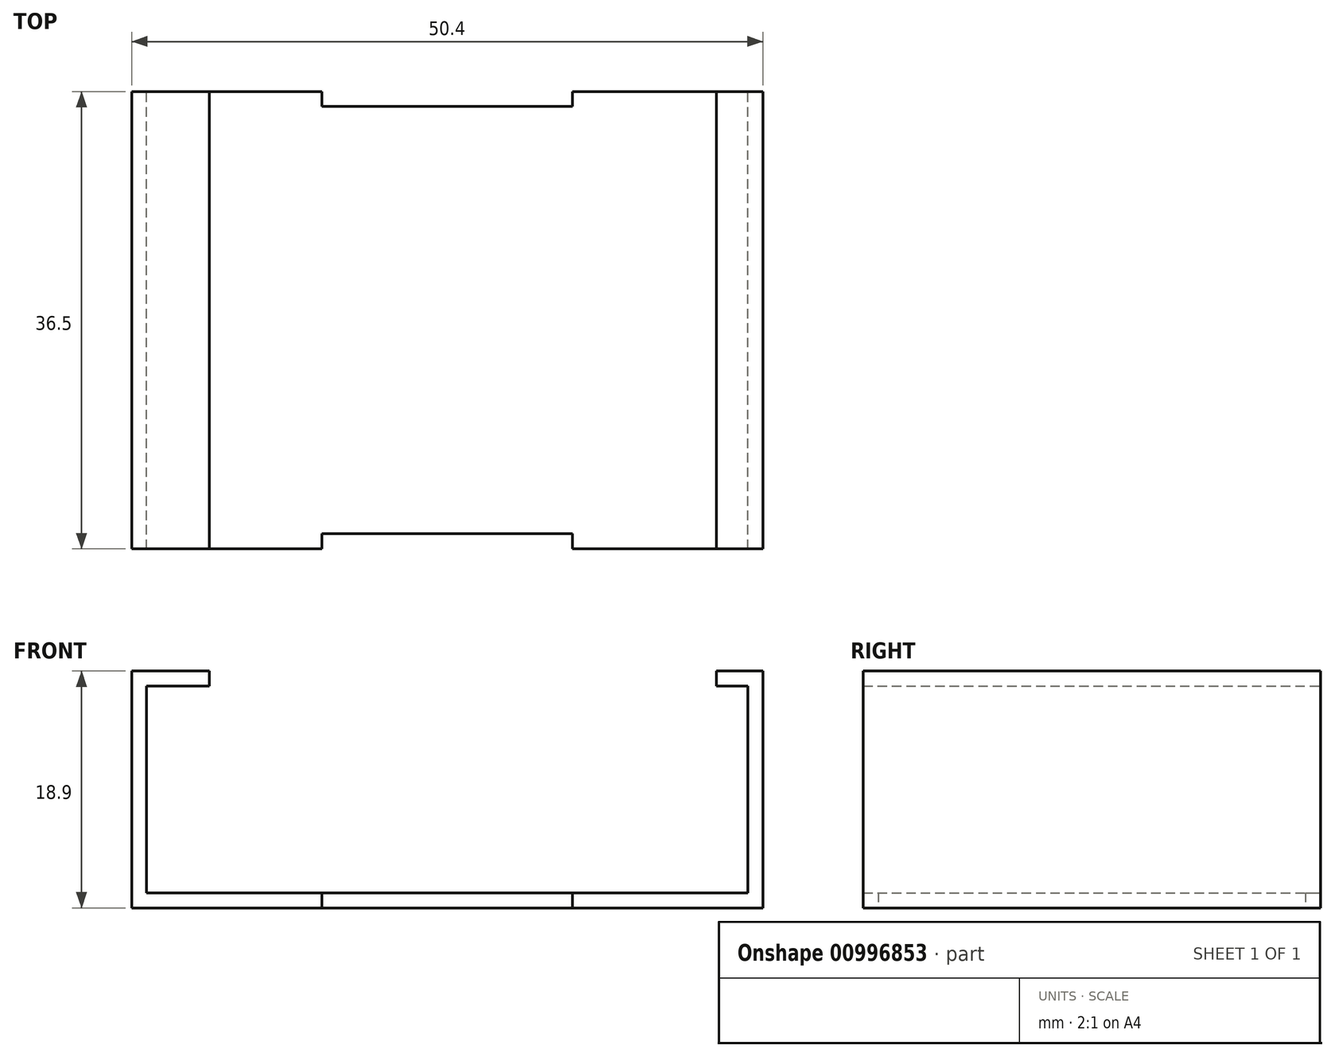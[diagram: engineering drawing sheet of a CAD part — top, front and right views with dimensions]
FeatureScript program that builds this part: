
annotation { "Feature Type Name" : "Feature", "Feature Type Description" : "" }
export const myFeature = defineFeature(function(context is Context, id is Id, definition is map)
    precondition{}
    {
        {
            var Q0;
            Q0=qCreatedBy(makeId("Top.planeOp"),FACE);
            var sketch = newSketch(context, id + "F0", { "sketchPlane" : qUnion([Q0])});
            skLineSegment(sketch, "E0.bottom", {"start": v(24, -18.25) * mm, "end": v(10, -18.25) * mm});
            skLineSegment(sketch, "E0.top", {"start": v(24, 18.25) * mm, "end": v(10, 18.25) * mm});
            skLineSegment(sketch, "E0.left", {"start": v(24, -18.25) * mm, "end": v(24, 18.25) * mm});
            skLineSegment(sketch, "E0.right", {"start": v(-24, -18.25) * mm, "end": v(-24, 18.25) * mm});
            skPoint(sketch, "E0.middle", {"position": v(0, 0) * mm});
            skLineSegment(sketch, "E1.bottom", {"start": v(10, 17.05) * mm, "end": v(-10, 17.05) * mm});
            skLineSegment(sketch, "E1.left", {"start": v(10, 17.05) * mm, "end": v(10, 18.25) * mm});
            skLineSegment(sketch, "E1.right", {"start": v(-10, 17.05) * mm, "end": v(-10, 18.25) * mm});
            skPoint(sketch, "E1.middle", {"position": v(0, 18.25) * mm});
            skLineSegment(sketch, "E2.top", {"start": v(10, -17.05) * mm, "end": v(-10, -17.05) * mm});
            skLineSegment(sketch, "E2.left", {"start": v(10, -18.25) * mm, "end": v(10, -17.05) * mm});
            skLineSegment(sketch, "E2.right", {"start": v(-10, -18.25) * mm, "end": v(-10, -17.05) * mm});
            skPoint(sketch, "E2.middle", {"position": v(0, -18.25) * mm});
            skLineSegment(sketch, "E3.trimOffspring", {"start": v(-10, 18.25) * mm, "end": v(-24, 18.25) * mm});
            skPoint(sketch, "E1.top.end.orphan", {"position": v(-10, 19.45) * mm});
            skPoint(sketch, "E4.orphan", {"position": v(10, 19.45) * mm});
            skPoint(sketch, "E2.bottom.end.orphan", {"position": v(-10, -19.45) * mm});
            skPoint(sketch, "E5.orphan", {"position": v(10, -19.45) * mm});
            skLineSegment(sketch, "E6.trimOffspring", {"start": v(-10, -18.25) * mm, "end": v(-24, -18.25) * mm});
            skLineSegment(sketch, "E7.bottom", {"start": v(24, 18.25) * mm, "end": v(25.2, 18.25) * mm});
            skLineSegment(sketch, "E7.top", {"start": v(24, -18.25) * mm, "end": v(25.2, -18.25) * mm});
            skLineSegment(sketch, "E7.left", {"start": v(24, 18.25) * mm, "end": v(24, -18.25) * mm});
            skLineSegment(sketch, "E7.right", {"start": v(25.2, 18.25) * mm, "end": v(25.2, -18.25) * mm});
            skLineSegment(sketch, "E8.bottom", {"start": v(-24, -18.25) * mm, "end": v(-25.2, -18.25) * mm});
            skLineSegment(sketch, "E8.top", {"start": v(-24, 18.25) * mm, "end": v(-25.2, 18.25) * mm});
            skLineSegment(sketch, "E8.right", {"start": v(-25.2, -18.25) * mm, "end": v(-25.2, 18.25) * mm});
            skSolve(sketch);
        }
        {
            var Q0;
            Q0=makeQuery(id+"F0.imprint","IMPRINT",FACE,{"disambiguationData":[TD([[makeQuery(id+"F0.imprint","IMPRINT",EDGE,{"derivedFrom":sQuery(id+"F0.wireOp",EDGE,"E0.bottom")}),-1.0]])]});
            extrude(context, id + "F1", {"entities" : qUnion([Q0]), "depth" : 1.2 * mm, "offsetDistance" : 25 * mm});
        }
        {
            var Q0;
            Q0=makeQuery(id+"F0.imprint","IMPRINT",FACE,{"disambiguationData":[TD([[makeQuery(id+"F0.imprint","IMPRINT",EDGE,{"derivedFrom":sQuery(id+"F0.wireOp",EDGE,"E8.bottom")}),-1.0]])]});
            var Q1;
            Q1=makeQuery(id+"F0.imprint","IMPRINT",FACE,{"disambiguationData":[TD([[makeQuery(id+"F0.imprint","IMPRINT",EDGE,{"derivedFrom":sQuery(id+"F0.wireOp",EDGE,"E7.bottom")}),-1.0]])]});
            extrude(context, id + "F2", {"entities" : qUnion([Q0, Q1]), "operationType" : NewBodyOperationType.ADD, "depth" : (16.5 + 1.2) * mm, "offsetDistance" : 25 * mm});
        }
        {
            var Q0;
            Q0=makeQuery(id+"F2.opExtrude","CAP_FACE",FACE,{"disambiguationData":[OSD([sQuery(id+"F0.wireOp",EDGE,"E8.bottom"),sQuery(id+"F0.wireOp",EDGE,"E8.top"),sQuery(id+"F0.wireOp",EDGE,"E0.right"),sQuery(id+"F0.wireOp",EDGE,"E8.right")])],"isStart":false});
            var sketch = newSketch(context, id + "F3", { "sketchPlane" : qUnion([Q0])});
            skLineSegment(sketch, "E9.bottom", {"start": v(-25.2, 18.25) * mm, "end": v(-19, 18.25) * mm});
            skLineSegment(sketch, "E9.top", {"start": v(-25.2, -18.25) * mm, "end": v(-19, -18.25) * mm});
            skLineSegment(sketch, "E9.left", {"start": v(-25.2, 18.25) * mm, "end": v(-25.2, -18.25) * mm});
            skLineSegment(sketch, "E9.right", {"start": v(-19, 18.25) * mm, "end": v(-19, -18.25) * mm});
            skLineSegment(sketch, "E10.bottom", {"start": v(25.2, -18.25) * mm, "end": v(21.5, -18.25) * mm});
            skLineSegment(sketch, "E10.top", {"start": v(25.2, 18.25) * mm, "end": v(21.5, 18.25) * mm});
            skLineSegment(sketch, "E10.left", {"start": v(25.2, -18.25) * mm, "end": v(25.2, 18.25) * mm});
            skLineSegment(sketch, "E10.right", {"start": v(21.5, -18.25) * mm, "end": v(21.5, 18.25) * mm});
            skSolve(sketch);
        }
        {
            var Q0;
            {var subQ2=sQuery(id+"F3.wireOp",EDGE,"E9.left");Q0=makeQuery(id+"F3.imprint","IMPRINT",FACE,{"disambiguationData":[TD([[makeQuery(id+"F3.imprint","IMPRINT",EDGE,{"derivedFrom":subQ2}),-1.0]])]});}
            var Q1;
            {var subQ2=sQuery(id+"F3.wireOp",EDGE,"E9.right");Q1=makeQuery(id+"F3.imprint","IMPRINT",FACE,{"disambiguationData":[TD([[makeQuery(id+"F3.imprint","IMPRINT",EDGE,{"derivedFrom":subQ2}),-1.0]])]});}
            var Q2;
            Q2=makeQuery(id+"F3.imprint","IMPRINT",FACE,{"disambiguationData":[TD([[makeQuery(id+"F3.imprint","IMPRINT",EDGE,{"derivedFrom":sQuery(id+"F3.wireOp",EDGE,"E10.bottom")}),-1.0]])]});
            extrude(context, id + "F4", {"entities" : qUnion([Q0, Q1, Q2]), "operationType" : NewBodyOperationType.ADD, "depth" : 1.2 * mm, "offsetDistance" : 25 * mm});
        }
    });
